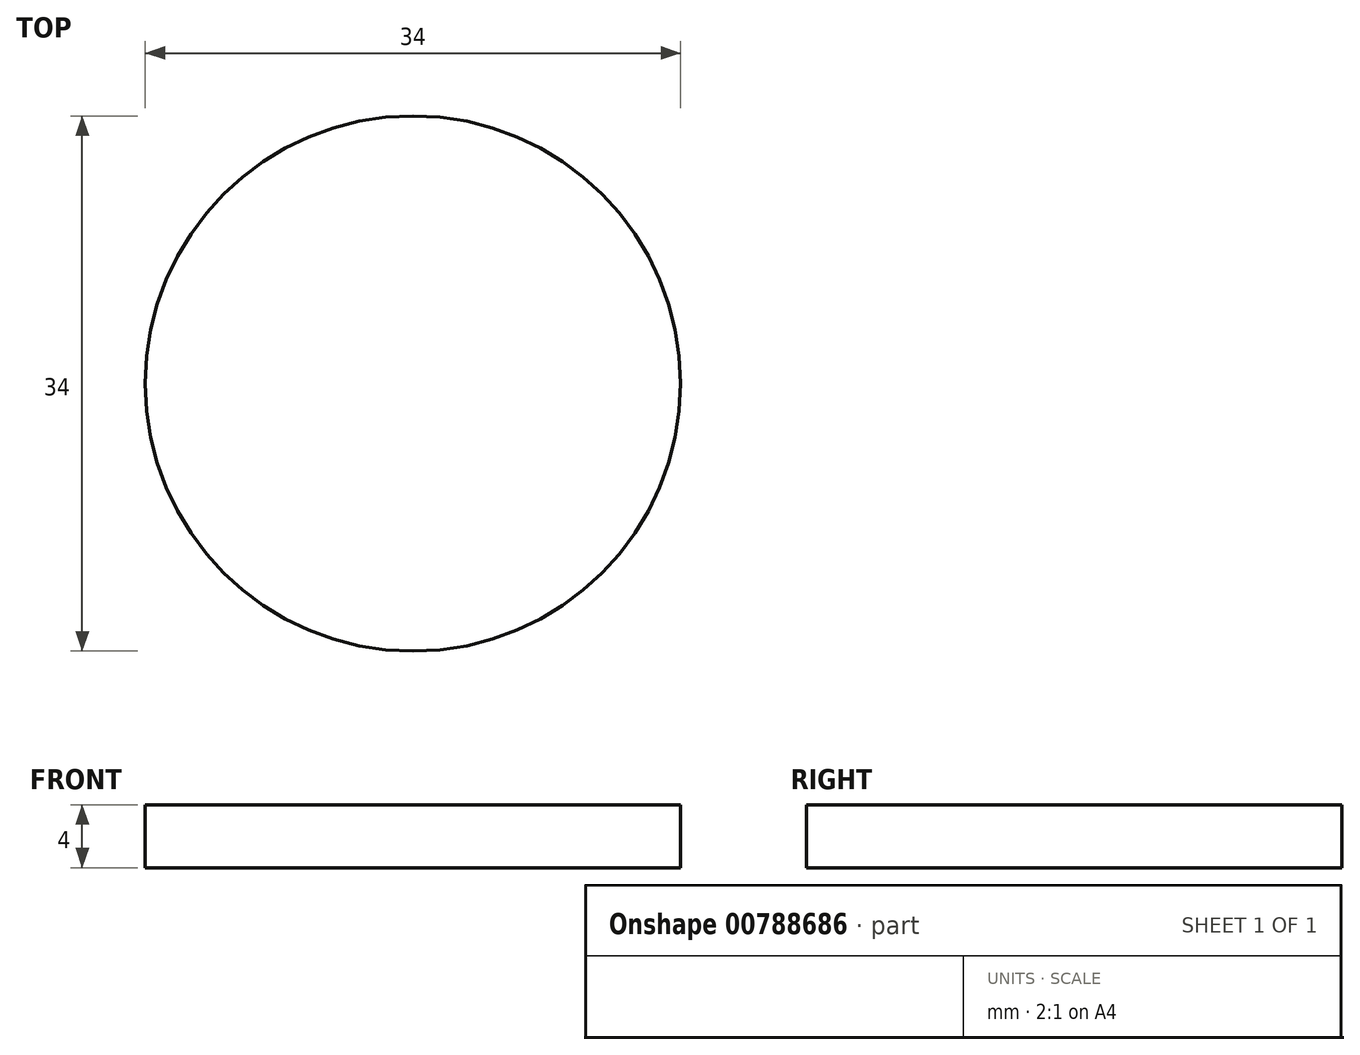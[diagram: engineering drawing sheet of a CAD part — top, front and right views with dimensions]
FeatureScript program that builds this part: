
annotation { "Feature Type Name" : "Feature", "Feature Type Description" : "" }
export const myFeature = defineFeature(function(context is Context, id is Id, definition is map)
    precondition{}
    {
        {
            var Q0;
            Q0=qCreatedBy(makeId("Top.planeOp"),FACE);
            var sketch = newSketch(context, id + "F0", { "sketchPlane" : qUnion([Q0])});
            skCircle(sketch, "E0", {"center": v(0, 0) * mm, "radius": 17 * mm});
            skSolve(sketch);
        }
        {
            var Q0;
            Q0 = qSketchRegion(id + "F0", true);
            extrude(context, id + "F1", {"entities" : qUnion([Q0]), "depth" : 4 * mm, "offsetDistance" : 25 * mm});
        }
    });
